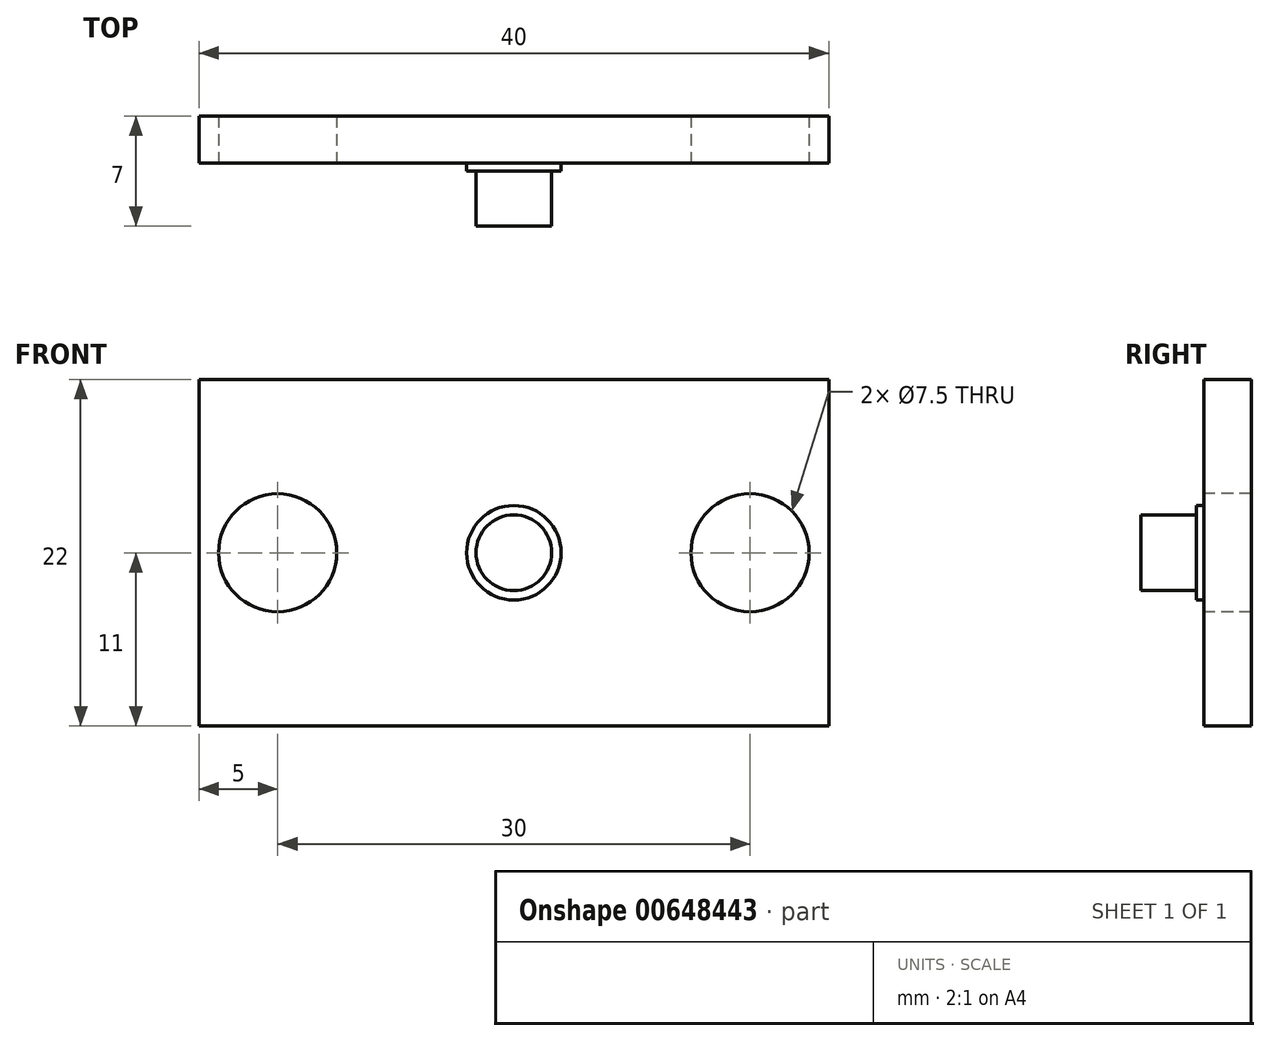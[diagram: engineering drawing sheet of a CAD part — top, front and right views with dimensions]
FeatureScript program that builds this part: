
annotation { "Feature Type Name" : "Feature", "Feature Type Description" : "" }
export const myFeature = defineFeature(function(context is Context, id is Id, definition is map)
    precondition{}
    {
        {
            var Q0;
            Q0=qCreatedBy(makeId("Front.planeOp"),FACE);
            var sketch = newSketch(context, id + "F0", { "sketchPlane" : qUnion([Q0])});
            skLineSegment(sketch, "E0.bottom", {"start": v(0, 0) * mm, "end": v(40, 0) * mm});
            skLineSegment(sketch, "E0.top", {"start": v(0, 22) * mm, "end": v(40, 22) * mm});
            skLineSegment(sketch, "E0.left", {"start": v(0, 0) * mm, "end": v(0, 22) * mm});
            skLineSegment(sketch, "E0.right", {"start": v(40, 0) * mm, "end": v(40, 22) * mm});
            skSolve(sketch);
        }
        {
            var Q0;
            Q0=makeQuery(id+"F0.imprint","IMPRINT",FACE,{"disambiguationData":[TD([[makeQuery(id+"F0.imprint","IMPRINT",EDGE,{"derivedFrom":sQuery(id+"F0.wireOp",EDGE,"E0.bottom")}),1.0]])]});
            extrude(context, id + "F1", {"entities" : qUnion([Q0]), "depth" : 3 * mm, "offsetDistance" : 25 * mm});
        }
        {
            var Q0;
            Q0=makeQuery(id+"F1.opExtrude","CAP_FACE",FACE,{"disambiguationData":[OSD([sQuery(id+"F0.wireOp",EDGE,"E0.bottom"),sQuery(id+"F0.wireOp",EDGE,"E0.top"),sQuery(id+"F0.wireOp",EDGE,"E0.left"),sQuery(id+"F0.wireOp",EDGE,"E0.right")])],"isStart":false});
            var sketch = newSketch(context, id + "F2", { "sketchPlane" : qUnion([Q0])});
            skCircle(sketch, "E1", {"center": v(20, 11) * mm, "radius": 3 * mm});
            skSolve(sketch);
        }
        {
            var Q0;
            Q0=makeQuery(id+"F2.imprint","IMPRINT",FACE,{"disambiguationData":[TD([[makeQuery(id+"F2.imprint","IMPRINT",EDGE,{"derivedFrom":sQuery(id+"F2.wireOp",EDGE,"E1")}),1.0]])]});
            extrude(context, id + "F3", {"entities" : qUnion([Q0]), "operationType" : NewBodyOperationType.ADD, "depth" : 0.5 * mm, "offsetDistance" : 25 * mm});
        }
        {
            var Q0;
            Q0=makeQuery(id+"F3.opExtrude","CAP_FACE",FACE,{"disambiguationData":[OSD([sQuery(id+"F2.wireOp",EDGE,"E1")])],"isStart":false});
            var sketch = newSketch(context, id + "F4", { "sketchPlane" : qUnion([Q0])});
            skCircle(sketch, "E2.0.0", {"center": v(20, 11) * mm, "radius": 3 * mm});
            skCircle(sketch, "E3", {"center": v(20, 11) * mm, "radius": 2.4 * mm});
            skSolve(sketch);
        }
        {
            var Q0;
            Q0=makeQuery(id+"F4.imprint","IMPRINT",FACE,{"disambiguationData":[TD([[makeQuery(id+"F4.imprint","IMPRINT",EDGE,{"derivedFrom":sQuery(id+"F4.wireOp",EDGE,"E3")}),1.0]])]});
            extrude(context, id + "F5", {"entities" : qUnion([Q0]), "operationType" : NewBodyOperationType.ADD, "depth" : 3.5 * mm, "offsetDistance" : 25 * mm});
        }
        {
            var Q0;
            Q0=makeQuery(id+"F1.opExtrude","CAP_FACE",FACE,{"disambiguationData":[OSD([sQuery(id+"F0.wireOp",EDGE,"E0.bottom"),sQuery(id+"F0.wireOp",EDGE,"E0.top"),sQuery(id+"F0.wireOp",EDGE,"E0.left"),sQuery(id+"F0.wireOp",EDGE,"E0.right")])],"isStart":false});
            var sketch = newSketch(context, id + "F6", { "sketchPlane" : qUnion([Q0])});
            skCircle(sketch, "E4", {"center": v(5, 11) * mm, "radius": 3.75 * mm});
            skCircle(sketch, "E5", {"center": v(35, 11) * mm, "radius": 3.75 * mm});
            skCircle(sketch, "E6.0.0", {"center": v(20, 11) * mm, "radius": 2.4 * mm});
            skSolve(sketch);
        }
        {
            var Q0;
            Q0=makeQuery(id+"F6.imprint","IMPRINT",FACE,{"disambiguationData":[TD([[makeQuery(id+"F6.imprint","IMPRINT",EDGE,{"derivedFrom":sQuery(id+"F6.wireOp",EDGE,"E4")}),1.0]])]});
            var Q1;
            Q1=makeQuery(id+"F6.imprint","IMPRINT",FACE,{"disambiguationData":[TD([[makeQuery(id+"F6.imprint","IMPRINT",EDGE,{"derivedFrom":sQuery(id+"F6.wireOp",EDGE,"E5")}),1.0]])]});
            extrude(context, id + "F7", {"entities" : qUnion([Q0, Q1]), "operationType" : NewBodyOperationType.REMOVE, "oppositeDirection" : true, "depth" : 25 * mm, "offsetDistance" : 25 * mm});
        }
    });
